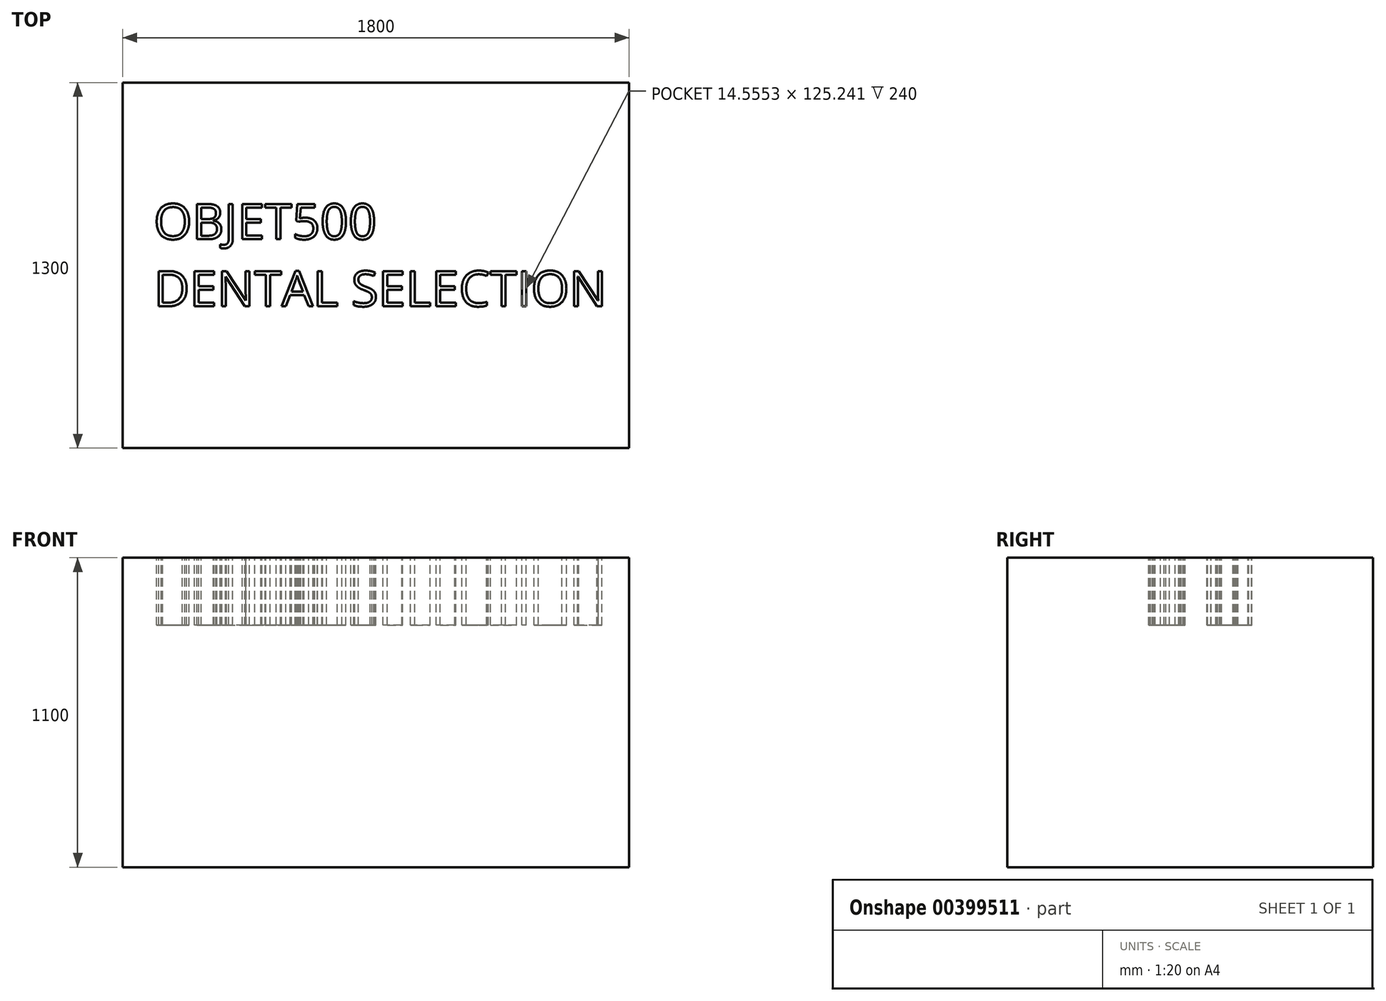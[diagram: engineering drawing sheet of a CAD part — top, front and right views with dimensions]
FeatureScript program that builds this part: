
annotation { "Feature Type Name" : "Feature", "Feature Type Description" : "" }
export const myFeature = defineFeature(function(context is Context, id is Id, definition is map)
    precondition{}
    {
        {
            var Q0;
            Q0=qCreatedBy(makeId("Top.planeOp"),FACE);
            var sketch = newSketch(context, id + "F0", { "sketchPlane" : qUnion([Q0])});
            skLineSegment(sketch, "E0.bottom", {"start": v(900, -650) * mm, "end": v(-900, -650) * mm});
            skLineSegment(sketch, "E0.top", {"start": v(900, 650) * mm, "end": v(-900, 650) * mm});
            skLineSegment(sketch, "E0.left", {"start": v(900, -650) * mm, "end": v(900, 650) * mm});
            skLineSegment(sketch, "E0.right", {"start": v(-900, -650) * mm, "end": v(-900, 650) * mm});
            skPoint(sketch, "E0.middle", {"position": v(0, 0) * mm});
            skSolve(sketch);
        }
        {
            var Q0;
            Q0 = qSketchRegion(id + "F0", true);
            extrude(context, id + "F1", {"entities" : qUnion([Q0]), "depth" : 1100 * mm});
        }
        {
            var Q0;
            Q0=makeQuery(id+"F1.opExtrude","CAP_FACE",FACE,{"disambiguationData":[OSD([sQuery(id+"F0.wireOp",EDGE,"E0.bottom"),sQuery(id+"F0.wireOp",EDGE,"E0.top"),sQuery(id+"F0.wireOp",EDGE,"E0.left"),sQuery(id+"F0.wireOp",EDGE,"E0.right")])],"isStart":false});
            var sketch = newSketch(context, id + "F2", { "sketchPlane" : qUnion([Q0])});
            skText(sketch, "E1", { "text": "OBJET500\nDENTAL SELECTION", "fontName": "OpenSans-Regular.ttf"});
            const initialGuessF2  = {"E1": [-0.79, 0.09301, 1, 0, 0.12631]};
            skSetInitialGuess(sketch, initialGuessF2);
            skSolve(sketch);
        }
        {
            var Q0;
            Q0 = qSketchRegion(id + "F2", true);
            extrude(context, id + "F3", {"entities" : qUnion([Q0]), "operationType" : NewBodyOperationType.REMOVE, "oppositeDirection" : true, "depth" : 240 * mm});
        }
    });
